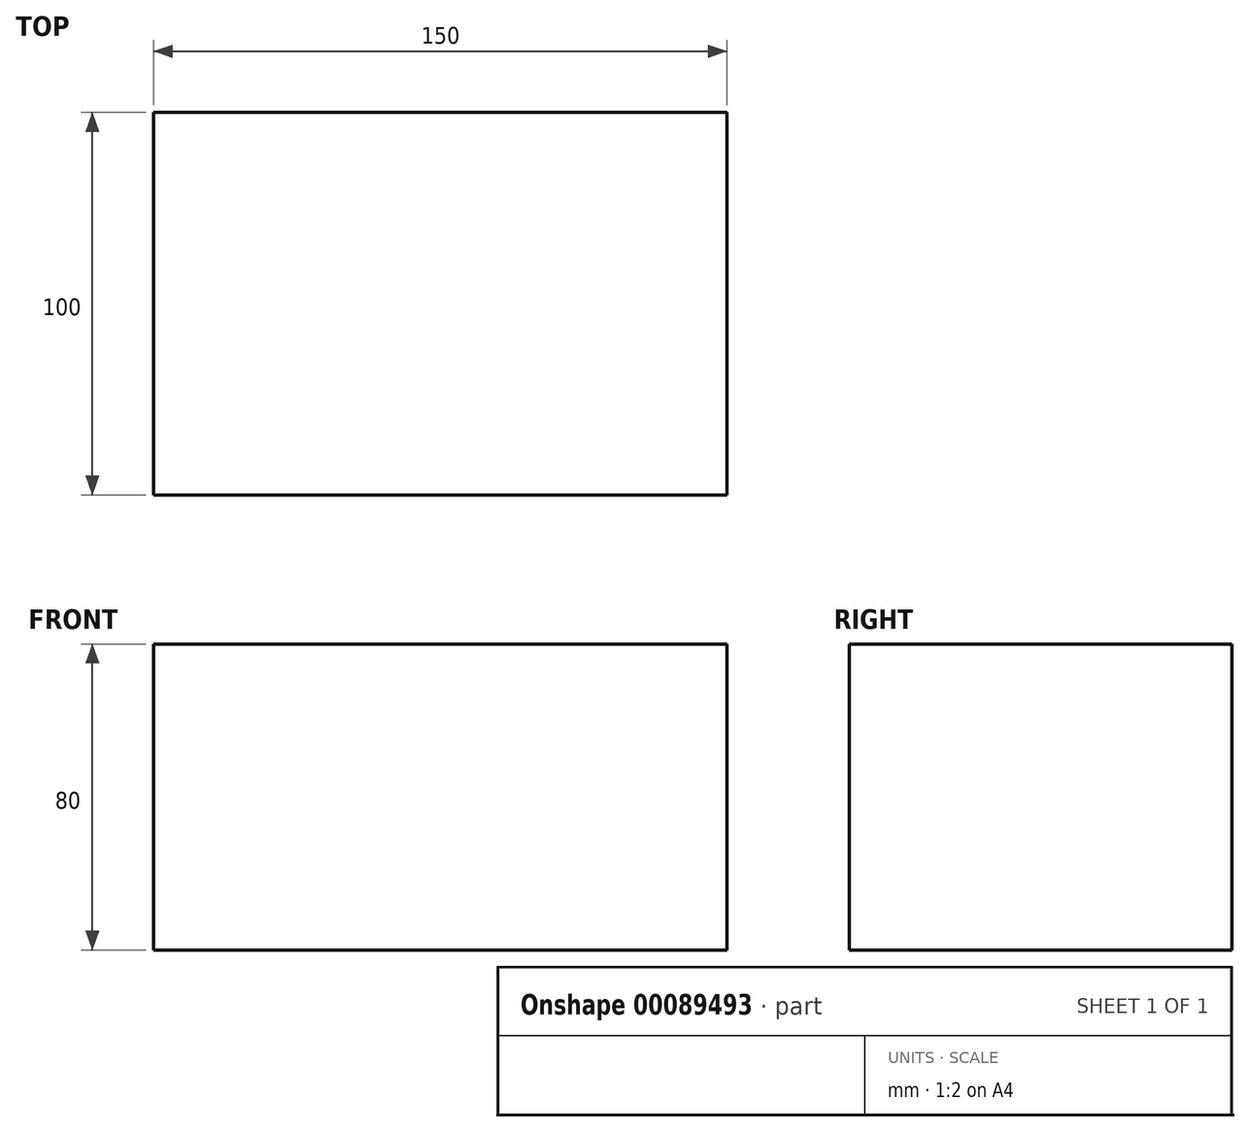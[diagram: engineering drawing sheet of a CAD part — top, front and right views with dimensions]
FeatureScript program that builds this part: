
annotation { "Feature Type Name" : "Feature", "Feature Type Description" : "" }
export const myFeature = defineFeature(function(context is Context, id is Id, definition is map)
    precondition{}
    {
        {
            var Q0;
            Q0=qCreatedBy(makeId("Top.planeOp"),FACE);
            var sketch = newSketch(context, id + "F0", { "sketchPlane" : qUnion([Q0])});
            skLineSegment(sketch, "E0.bottom", {"start": v(75, -50) * mm, "end": v(-75, -50) * mm});
            skLineSegment(sketch, "E0.top", {"start": v(75, 50) * mm, "end": v(-75, 50) * mm});
            skLineSegment(sketch, "E0.left", {"start": v(75, -50) * mm, "end": v(75, 50) * mm});
            skLineSegment(sketch, "E0.right", {"start": v(-75, -50) * mm, "end": v(-75, 50) * mm});
            skPoint(sketch, "E0.middle", {"position": v(0, 0) * mm});
            skSolve(sketch);
        }
        {
            var Q0;
            Q0=makeQuery(id+"F0.imprint","IMPRINT",FACE,{"disambiguationData":[TD([[makeQuery(id+"F0.imprint","IMPRINT",EDGE,{"derivedFrom":sQuery(id+"F0.wireOp",EDGE,"E0.bottom")}),-1.0]])]});
            extrude(context, id + "F1", {"entities" : qUnion([Q0]), "depth" : 80 * mm});
        }
    });
